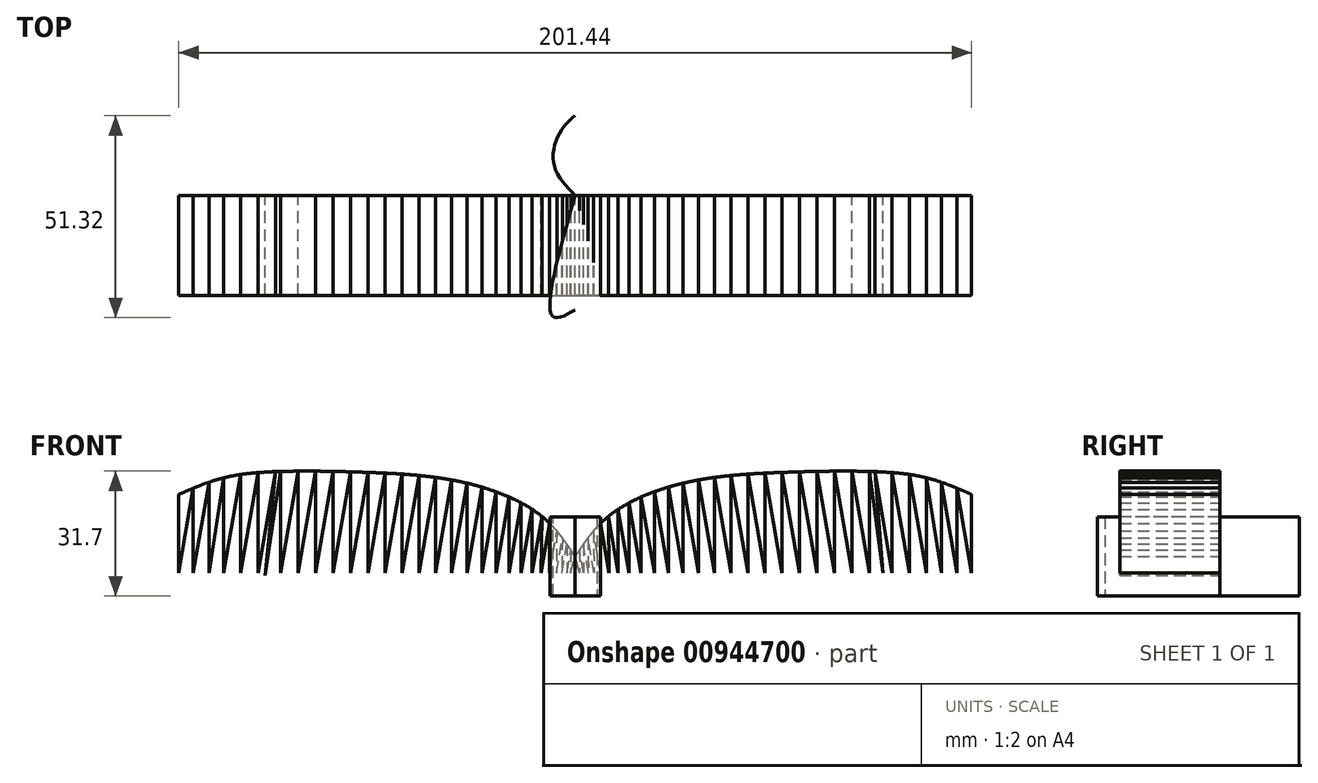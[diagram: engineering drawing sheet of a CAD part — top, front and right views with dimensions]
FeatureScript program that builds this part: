
annotation { "Feature Type Name" : "Feature", "Feature Type Description" : "" }
export const myFeature = defineFeature(function(context is Context, id is Id, definition is map)
    precondition{}
    {
        {
            var Q0;
            Q0=qCreatedBy(makeId("Front.planeOp"),FACE);
            var sketch = newSketch(context, id + "F0", { "sketchPlane" : qUnion([Q0]), "disableImprinting" : false});
            skFitSpline(sketch, "E0", {"points": [v(0, 0) * mm, v(-8.64, 10.35) * mm, v(-28.14, 18.8) * mm, v(-53.68, 21.4) * mm, v(-74.78, 21.61) * mm, v(-89.26, 20) * mm, v(-100.72, 15.78) * mm], "startDerivative": vector(-49.5, 75.28) * mm, "endDerivative": vector(-80.54, -34.92) * mm});
            skLineSegment(sketch, "E1", {"start": v(-100.72, 15.78) * mm, "end": v(-100.72, -4.12) * mm});
            skLineSegment(sketch, "E2", {"start": v(-100.72, -4.12) * mm, "end": v(-97, 17.4) * mm});
            skLineSegment(sketch, "E3", {"start": v(-97, 17.4) * mm, "end": v(-97, -4.12) * mm});
            skLineSegment(sketch, "E4", {"start": v(-97, -4.12) * mm, "end": v(-93.03, 18.88) * mm});
            skLineSegment(sketch, "E5", {"start": v(-93.03, 18.88) * mm, "end": v(-93.03, -4.12) * mm});
            skLineSegment(sketch, "E6", {"start": v(-93.03, -4.12) * mm, "end": v(-89.26, 20) * mm});
            skLineSegment(sketch, "E7", {"start": v(-89.26, 20) * mm, "end": v(-89.26, -4.12) * mm});
            skLineSegment(sketch, "E8", {"start": v(-89.26, -4.12) * mm, "end": v(-84.95, 20.84) * mm});
            skLineSegment(sketch, "E9", {"start": v(-84.95, 20.84) * mm, "end": v(-84.95, -4.12) * mm});
            skLineSegment(sketch, "E10", {"start": v(-84.95, -4.12) * mm, "end": v(-80.55, 21.32) * mm});
            skLineSegment(sketch, "E11", {"start": v(-80.55, 21.32) * mm, "end": v(-80.55, -4.12) * mm});
            skLineSegment(sketch, "E12", {"start": v(-80.55, -4.12) * mm, "end": v(-76.1, 21.61) * mm});
            skLineSegment(sketch, "E13", {"start": v(-74.78, 21.61) * mm, "end": v(-74.78, -4.12) * mm});
            skLineSegment(sketch, "E14", {"start": v(-74.78, -4.12) * mm, "end": v(-70.34, 21.61) * mm});
            skLineSegment(sketch, "E15", {"start": v(-70.34, 21.61) * mm, "end": v(-70.34, -4.12) * mm});
            skLineSegment(sketch, "E16", {"start": v(-70.34, -4.12) * mm, "end": v(-65.88, 21.69) * mm});
            skLineSegment(sketch, "E17", {"start": v(-65.88, 21.69) * mm, "end": v(-65.88, -4.12) * mm});
            skLineSegment(sketch, "E18", {"start": v(-65.88, -4.12) * mm, "end": v(-61.44, 21.62) * mm});
            skLineSegment(sketch, "E19", {"start": v(-61.44, 21.62) * mm, "end": v(-61.44, -4.12) * mm});
            skLineSegment(sketch, "E20", {"start": v(-61.44, -4.12) * mm, "end": v(-57, 21.52) * mm});
            skLineSegment(sketch, "E21", {"start": v(-57, 21.52) * mm, "end": v(-57, -4.12) * mm});
            skLineSegment(sketch, "E22", {"start": v(-57, -4.12) * mm, "end": v(-52.6, 21.37) * mm});
            skLineSegment(sketch, "E23", {"start": v(-52.6, 21.37) * mm, "end": v(-52.6, -4.12) * mm});
            skLineSegment(sketch, "E24", {"start": v(-52.6, -4.12) * mm, "end": v(-48.24, 21.2) * mm});
            skLineSegment(sketch, "E25", {"start": v(-48.24, 21.2) * mm, "end": v(-48.24, -4.12) * mm});
            skLineSegment(sketch, "E26", {"start": v(-48.24, -4.12) * mm, "end": v(-43.9, 20.94) * mm});
            skLineSegment(sketch, "E27", {"start": v(-43.9, 20.94) * mm, "end": v(-43.9, -4.12) * mm});
            skLineSegment(sketch, "E28", {"start": v(-43.9, -4.12) * mm, "end": v(-39.64, 20.58) * mm});
            skLineSegment(sketch, "E29", {"start": v(-39.64, 20.58) * mm, "end": v(-39.64, -4.12) * mm});
            skLineSegment(sketch, "E30", {"start": v(-39.64, -4.12) * mm, "end": v(-35.46, 20.1) * mm});
            skLineSegment(sketch, "E31", {"start": v(-35.46, 20.1) * mm, "end": v(-35.46, -4.12) * mm});
            skLineSegment(sketch, "E32", {"start": v(-35.46, -4.12) * mm, "end": v(-31.39, 19.46) * mm});
            skLineSegment(sketch, "E33", {"start": v(-31.39, 19.46) * mm, "end": v(-31.39, -4.12) * mm});
            skLineSegment(sketch, "E34", {"start": v(-31.39, -4.12) * mm, "end": v(-27.43, 18.8) * mm});
            skLineSegment(sketch, "E35", {"start": v(-27.43, 18.8) * mm, "end": v(-27.43, -4.12) * mm});
            skLineSegment(sketch, "E36", {"start": v(-27.43, -4.12) * mm, "end": v(-23.67, 17.63) * mm});
            skLineSegment(sketch, "E37", {"start": v(-23.67, 17.63) * mm, "end": v(-23.67, -4.12) * mm});
            skLineSegment(sketch, "E38", {"start": v(-23.67, -4.12) * mm, "end": v(-20.12, 16.46) * mm});
            skLineSegment(sketch, "E39", {"start": v(-20.12, 16.46) * mm, "end": v(-20.12, -4.12) * mm});
            skLineSegment(sketch, "E40", {"start": v(-20.12, -4.12) * mm, "end": v(-16.8, 15.12) * mm});
            skLineSegment(sketch, "E41", {"start": v(-16.8, 15.12) * mm, "end": v(-16.8, -4.12) * mm});
            skLineSegment(sketch, "E42", {"start": v(-16.8, -4.12) * mm, "end": v(-13.73, 13.64) * mm});
            skLineSegment(sketch, "E43", {"start": v(-13.73, 13.64) * mm, "end": v(-13.73, -4.12) * mm});
            skLineSegment(sketch, "E44", {"start": v(-13.73, -4.12) * mm, "end": v(-10.94, 12) * mm});
            skLineSegment(sketch, "E45", {"start": v(-10.94, 12) * mm, "end": v(-10.94, -4.12) * mm});
            skLineSegment(sketch, "E46", {"start": v(-10.94, -4.12) * mm, "end": v(-8.47, 10.21) * mm});
            skLineSegment(sketch, "E47", {"start": v(-8.47, 10.21) * mm, "end": v(-8.64, -4.12) * mm});
            skLineSegment(sketch, "E48", {"start": v(-8.64, -4.12) * mm, "end": v(-6.48, 8.43) * mm});
            skLineSegment(sketch, "E49", {"start": v(-6.48, 8.43) * mm, "end": v(-6.48, -4.12) * mm});
            skLineSegment(sketch, "E50", {"start": v(-6.48, -4.12) * mm, "end": v(-4.65, 6.46) * mm});
            skLineSegment(sketch, "E51", {"start": v(-4.65, 6.46) * mm, "end": v(-4.78, -4.12) * mm});
            skLineSegment(sketch, "E52", {"start": v(-4.78, -4.12) * mm, "end": v(-3.25, 4.72) * mm});
            skLineSegment(sketch, "E53", {"start": v(-3.25, 4.72) * mm, "end": v(-3.36, -4.12) * mm});
            skLineSegment(sketch, "E54", {"start": v(-3.36, -4.12) * mm, "end": v(-2.1, 3.14) * mm});
            skLineSegment(sketch, "E55", {"start": v(-2.1, 3.14) * mm, "end": v(-2.1, -4.12) * mm});
            skLineSegment(sketch, "E56", {"start": v(-2.1, -4.12) * mm, "end": v(-1.1, 1.67) * mm});
            skLineSegment(sketch, "E57", {"start": v(-1.1, 1.67) * mm, "end": v(-1.18, -4.12) * mm});
            skLineSegment(sketch, "E58", {"start": v(-1.18, -4.12) * mm, "end": v(0, 0) * mm});
            skFitSpline(sketch, "E59.MirrorCS", {"points": [v(0, 0) * mm, v(8.64, 10.35) * mm, v(28.14, 18.8) * mm, v(53.68, 21.4) * mm, v(74.78, 21.61) * mm, v(89.26, 20) * mm, v(100.72, 15.78) * mm], "startDerivative": vector(49.5, 75.28) * mm, "endDerivative": vector(80.54, -34.92) * mm});
            skLineSegment(sketch, "E60.MirrorCS", {"start": v(100.72, 15.78) * mm, "end": v(100.72, -4.12) * mm});
            skLineSegment(sketch, "E61.MirrorCS", {"start": v(100.72, -4.12) * mm, "end": v(97, 17.4) * mm});
            skLineSegment(sketch, "E62.MirrorCS", {"start": v(97, 17.4) * mm, "end": v(97, -4.12) * mm});
            skLineSegment(sketch, "E63.MirrorCS", {"start": v(97, -4.12) * mm, "end": v(93.03, 18.88) * mm});
            skLineSegment(sketch, "E64.MirrorCS", {"start": v(93.03, 18.88) * mm, "end": v(93.03, -4.12) * mm});
            skLineSegment(sketch, "E65.MirrorCS", {"start": v(93.03, -4.12) * mm, "end": v(89.26, 20) * mm});
            skLineSegment(sketch, "E66.MirrorCS", {"start": v(89.26, 20) * mm, "end": v(89.26, -4.12) * mm});
            skLineSegment(sketch, "E67.MirrorCS", {"start": v(89.26, -4.12) * mm, "end": v(84.95, 20.84) * mm});
            skLineSegment(sketch, "E68.MirrorCS", {"start": v(84.95, 20.84) * mm, "end": v(84.95, -4.12) * mm});
            skLineSegment(sketch, "E69.MirrorCS", {"start": v(84.95, -4.12) * mm, "end": v(80.55, 21.32) * mm});
            skLineSegment(sketch, "E70.MirrorCS", {"start": v(80.55, 21.32) * mm, "end": v(80.55, -4.12) * mm});
            skLineSegment(sketch, "E71.MirrorCS", {"start": v(80.55, -4.12) * mm, "end": v(76.1, 21.61) * mm});
            skLineSegment(sketch, "E72.MirrorCS", {"start": v(74.78, 21.61) * mm, "end": v(74.78, -4.12) * mm});
            skLineSegment(sketch, "E73.MirrorCS", {"start": v(74.78, -4.12) * mm, "end": v(70.34, 21.61) * mm});
            skLineSegment(sketch, "E74.MirrorCS", {"start": v(70.34, 21.61) * mm, "end": v(70.34, -4.12) * mm});
            skLineSegment(sketch, "E75.MirrorCS", {"start": v(70.34, -4.12) * mm, "end": v(65.88, 21.69) * mm});
            skLineSegment(sketch, "E76.MirrorCS", {"start": v(65.88, 21.69) * mm, "end": v(65.88, -4.12) * mm});
            skLineSegment(sketch, "E77.MirrorCS", {"start": v(65.88, -4.12) * mm, "end": v(61.44, 21.62) * mm});
            skLineSegment(sketch, "E78.MirrorCS", {"start": v(61.44, 21.62) * mm, "end": v(61.44, -4.12) * mm});
            skLineSegment(sketch, "E79.MirrorCS", {"start": v(61.44, -4.12) * mm, "end": v(57, 21.52) * mm});
            skLineSegment(sketch, "E80.MirrorCS", {"start": v(57, 21.52) * mm, "end": v(57, -4.12) * mm});
            skLineSegment(sketch, "E81.MirrorCS", {"start": v(57, -4.12) * mm, "end": v(52.6, 21.37) * mm});
            skLineSegment(sketch, "E82.MirrorCS", {"start": v(52.6, 21.37) * mm, "end": v(52.6, -4.12) * mm});
            skLineSegment(sketch, "E83.MirrorCS", {"start": v(52.6, -4.12) * mm, "end": v(48.24, 21.2) * mm});
            skLineSegment(sketch, "E84.MirrorCS", {"start": v(48.24, 21.2) * mm, "end": v(48.24, -4.12) * mm});
            skLineSegment(sketch, "E85.MirrorCS", {"start": v(48.24, -4.12) * mm, "end": v(43.9, 20.94) * mm});
            skLineSegment(sketch, "E86.MirrorCS", {"start": v(43.9, 20.94) * mm, "end": v(43.9, -4.12) * mm});
            skLineSegment(sketch, "E87.MirrorCS", {"start": v(43.9, -4.12) * mm, "end": v(39.64, 20.58) * mm});
            skLineSegment(sketch, "E88.MirrorCS", {"start": v(39.64, 20.58) * mm, "end": v(39.64, -4.12) * mm});
            skLineSegment(sketch, "E89.MirrorCS", {"start": v(39.64, -4.12) * mm, "end": v(35.46, 20.1) * mm});
            skLineSegment(sketch, "E90.MirrorCS", {"start": v(35.46, 20.1) * mm, "end": v(35.46, -4.12) * mm});
            skLineSegment(sketch, "E91.MirrorCS", {"start": v(35.46, -4.12) * mm, "end": v(31.39, 19.46) * mm});
            skLineSegment(sketch, "E92.MirrorCS", {"start": v(31.39, 19.46) * mm, "end": v(31.39, -4.12) * mm});
            skLineSegment(sketch, "E93.MirrorCS", {"start": v(31.39, -4.12) * mm, "end": v(27.43, 18.8) * mm});
            skLineSegment(sketch, "E94.MirrorCS", {"start": v(27.43, 18.8) * mm, "end": v(27.43, -4.12) * mm});
            skLineSegment(sketch, "E95.MirrorCS", {"start": v(27.43, -4.12) * mm, "end": v(23.67, 17.63) * mm});
            skLineSegment(sketch, "E96.MirrorCS", {"start": v(23.67, 17.63) * mm, "end": v(23.67, -4.12) * mm});
            skLineSegment(sketch, "E97.MirrorCS", {"start": v(23.67, -4.12) * mm, "end": v(20.12, 16.46) * mm});
            skLineSegment(sketch, "E98.MirrorCS", {"start": v(20.12, 16.46) * mm, "end": v(20.12, -4.12) * mm});
            skLineSegment(sketch, "E99.MirrorCS", {"start": v(20.12, -4.12) * mm, "end": v(16.8, 15.12) * mm});
            skLineSegment(sketch, "E100.MirrorCS", {"start": v(16.8, 15.12) * mm, "end": v(16.8, -4.12) * mm});
            skLineSegment(sketch, "E101.MirrorCS", {"start": v(16.8, -4.12) * mm, "end": v(13.73, 13.64) * mm});
            skLineSegment(sketch, "E102.MirrorCS", {"start": v(13.73, 13.64) * mm, "end": v(13.73, -4.12) * mm});
            skLineSegment(sketch, "E103.MirrorCS", {"start": v(13.73, -4.12) * mm, "end": v(10.94, 12) * mm});
            skLineSegment(sketch, "E104.MirrorCS", {"start": v(10.94, 12) * mm, "end": v(10.94, -4.12) * mm});
            skLineSegment(sketch, "E105.MirrorCS", {"start": v(10.94, -4.12) * mm, "end": v(8.47, 10.21) * mm});
            skLineSegment(sketch, "E106.MirrorCS", {"start": v(8.47, 10.21) * mm, "end": v(8.64, -4.12) * mm});
            skLineSegment(sketch, "E107.MirrorCS", {"start": v(8.64, -4.12) * mm, "end": v(6.48, 8.43) * mm});
            skLineSegment(sketch, "E108.MirrorCS", {"start": v(6.48, 8.43) * mm, "end": v(6.48, -4.12) * mm});
            skLineSegment(sketch, "E109.MirrorCS", {"start": v(6.48, -4.12) * mm, "end": v(4.65, 6.46) * mm});
            skLineSegment(sketch, "E110.MirrorCS", {"start": v(4.65, 6.46) * mm, "end": v(4.78, -4.12) * mm});
            skLineSegment(sketch, "E111.MirrorCS", {"start": v(4.78, -4.12) * mm, "end": v(3.25, 4.72) * mm});
            skLineSegment(sketch, "E112.MirrorCS", {"start": v(3.25, 4.72) * mm, "end": v(3.36, -4.12) * mm});
            skLineSegment(sketch, "E113.MirrorCS", {"start": v(3.36, -4.12) * mm, "end": v(2.1, 3.14) * mm});
            skLineSegment(sketch, "E114.MirrorCS", {"start": v(1.1, 1.67) * mm, "end": v(1.18, -4.12) * mm});
            skLineSegment(sketch, "E115.MirrorCS", {"start": v(1.18, -4.12) * mm, "end": v(0, 0) * mm});
            skLineSegment(sketch, "E116.MirrorCS", {"start": v(2.1, 3.14) * mm, "end": v(2.1, -4.12) * mm});
            skLineSegment(sketch, "E117.MirrorCS", {"start": v(2.1, -4.12) * mm, "end": v(1.1, 1.67) * mm});
            skLineSegment(sketch, "E118", {"start": v(-76.1, 21.61) * mm, "end": v(-78.71, -4.8) * mm});
            skLineSegment(sketch, "E119", {"start": v(-78.71, -4.8) * mm, "end": v(-74.78, 21.61) * mm});
            skLineSegment(sketch, "E120", {"start": v(76.1, 21.61) * mm, "end": v(78.16, -4.12) * mm});
            skLineSegment(sketch, "E121", {"start": v(78.16, -4.12) * mm, "end": v(74.78, 21.61) * mm});
            skSolve(sketch);
        }
        {
            var Q0;
            Q0 = qSketchRegion(id + "F0", true);
            extrude(context, id + "F1", {"entities" : qUnion([Q0]), "flatOperationType" : FlatOperationType.REMOVE, "depth" : 25.4 * mm, "offsetDistance" : 25.4 * mm, "domain" : OperationDomain.MODEL});
        }
        {
            var Q0;
            Q0=qCreatedBy(makeId("Top.planeOp"),FACE);
            var sketch = newSketch(context, id + "F2", { "sketchPlane" : qUnion([Q0])});
            skLineSegment(sketch, "E122.left", {"start": v(-6.44, 14.6) * mm, "end": v(-6.44, 14.6) * mm});
            skLineSegment(sketch, "E122.right", {"start": v(-5.43, 14.6) * mm, "end": v(-5.43, 14.6) * mm});
            skLineSegment(sketch, "E123", {"start": v(0, 0) * mm, "end": v(0, 20.29) * mm});
            skFitSpline(sketch, "E124", {"points": [v(0, 0) * mm, v(-5.43, 8.01) * mm, v(-3.71, 16.29) * mm, v(0, 20.29) * mm], "startDerivative": vector(-19.34, 20.16) * mm, "endDerivative": vector(14.14, 11.9) * mm});
            skFitSpline(sketch, "E125.MirrorCS", {"points": [v(0, 0) * mm, v(5.43, 8.01) * mm, v(3.71, 16.29) * mm, v(0, 20.29) * mm], "startDerivative": vector(19.34, 20.16) * mm, "endDerivative": vector(-14.14, 11.9) * mm});
            skLineSegment(sketch, "E126", {"start": v(0, 0) * mm, "end": v(0, -29.12) * mm});
            skFitSpline(sketch, "E127", {"points": [v(0, 0) * mm, v(-5.7, -30.68) * mm, v(0, -29.12) * mm], "startDerivative": vector(-17.55, -61.15) * mm, "endDerivative": vector(22.86, 12.58) * mm});
            skFitSpline(sketch, "E128.MirrorCS", {"points": [v(0, 0) * mm, v(5.7, -30.68) * mm, v(0, -29.12) * mm], "startDerivative": vector(17.55, -61.15) * mm, "endDerivative": vector(-22.86, 12.58) * mm});
            skSolve(sketch);
        }
        {
            var Q0;
            Q0 = qSketchRegion(id + "F2", true);
            extrude(context, id + "F3", {"entities" : qUnion([Q0]), "depth" : 10 * mm, "offsetDistance" : 25.4 * mm, "hasSecondDirection" : true, "secondDirectionOppositeDirection" : true, "secondDirectionDepth" : 10 * mm});
        }
    });
